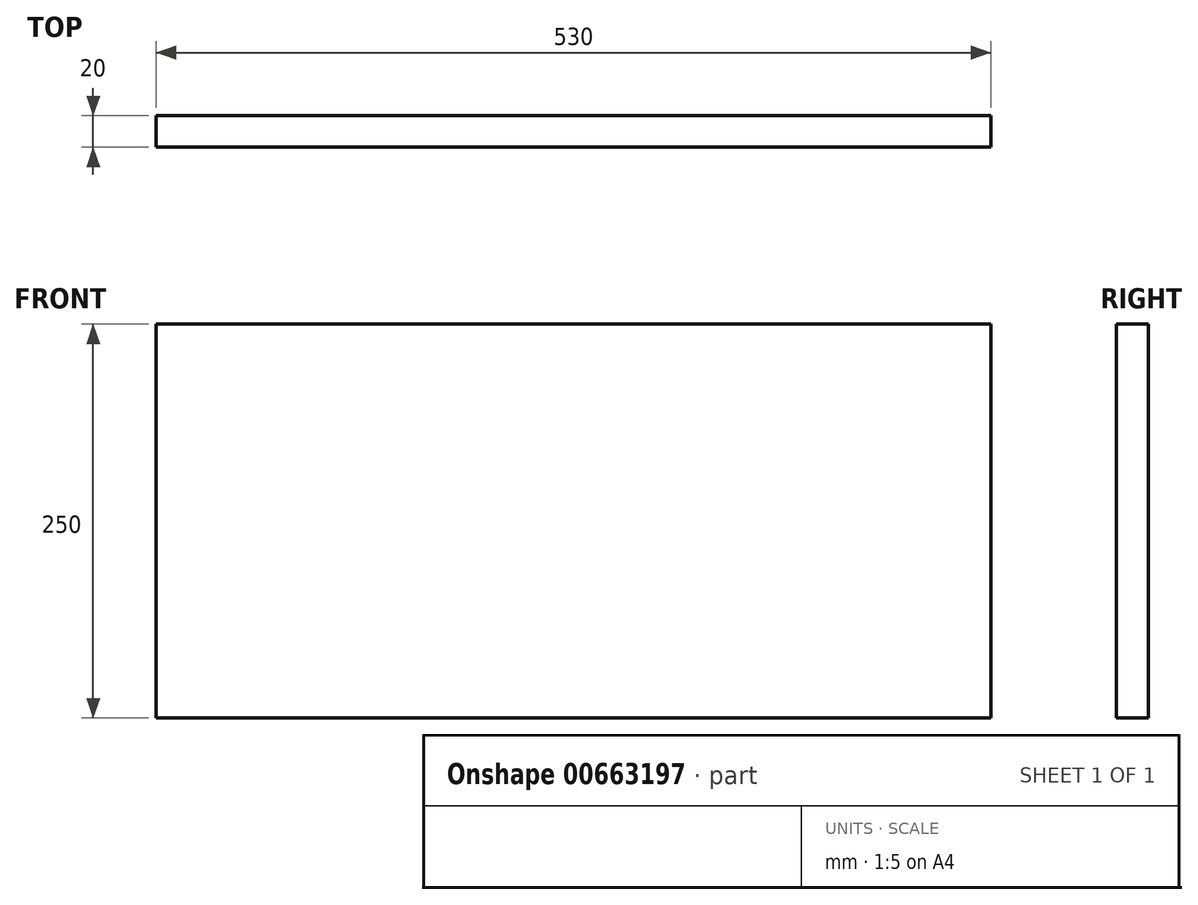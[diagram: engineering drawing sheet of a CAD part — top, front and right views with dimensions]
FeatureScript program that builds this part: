
annotation { "Feature Type Name" : "Feature", "Feature Type Description" : "" }
export const myFeature = defineFeature(function(context is Context, id is Id, definition is map)
    precondition{}
    {
        {
            var Q0;
            Q0=qCreatedBy(makeId("Top.planeOp"),FACE);
            var sketch = newSketch(context, id + "F0", { "sketchPlane" : qUnion([Q0])});
            skLineSegment(sketch, "E0.bottom", {"start": v(264.4, 10) * mm, "end": v(-265.6, 10) * mm});
            skLineSegment(sketch, "E0.top", {"start": v(264.4, -10) * mm, "end": v(-265.6, -10) * mm});
            skLineSegment(sketch, "E0.left", {"start": v(264.4, 10) * mm, "end": v(264.4, -10) * mm});
            skLineSegment(sketch, "E0.right", {"start": v(-265.6, 10) * mm, "end": v(-265.6, -10) * mm});
            skPoint(sketch, "E0.middle", {"position": v(-0.6, 0) * mm});
            skSolve(sketch);
        }
        {
            var Q0;
            Q0=makeQuery(id+"F0.imprint","IMPRINT",FACE,{"disambiguationData":[TD([[makeQuery(id+"F0.imprint","IMPRINT",EDGE,{"derivedFrom":sQuery(id+"F0.wireOp",EDGE,"E0.bottom")}),1.0]])]});
            extrude(context, id + "F1", {"entities" : qUnion([Q0]), "endBound" : BoundingType.SYMMETRIC, "depth" : 250 * mm, "offsetDistance" : 25 * mm});
        }
    });
